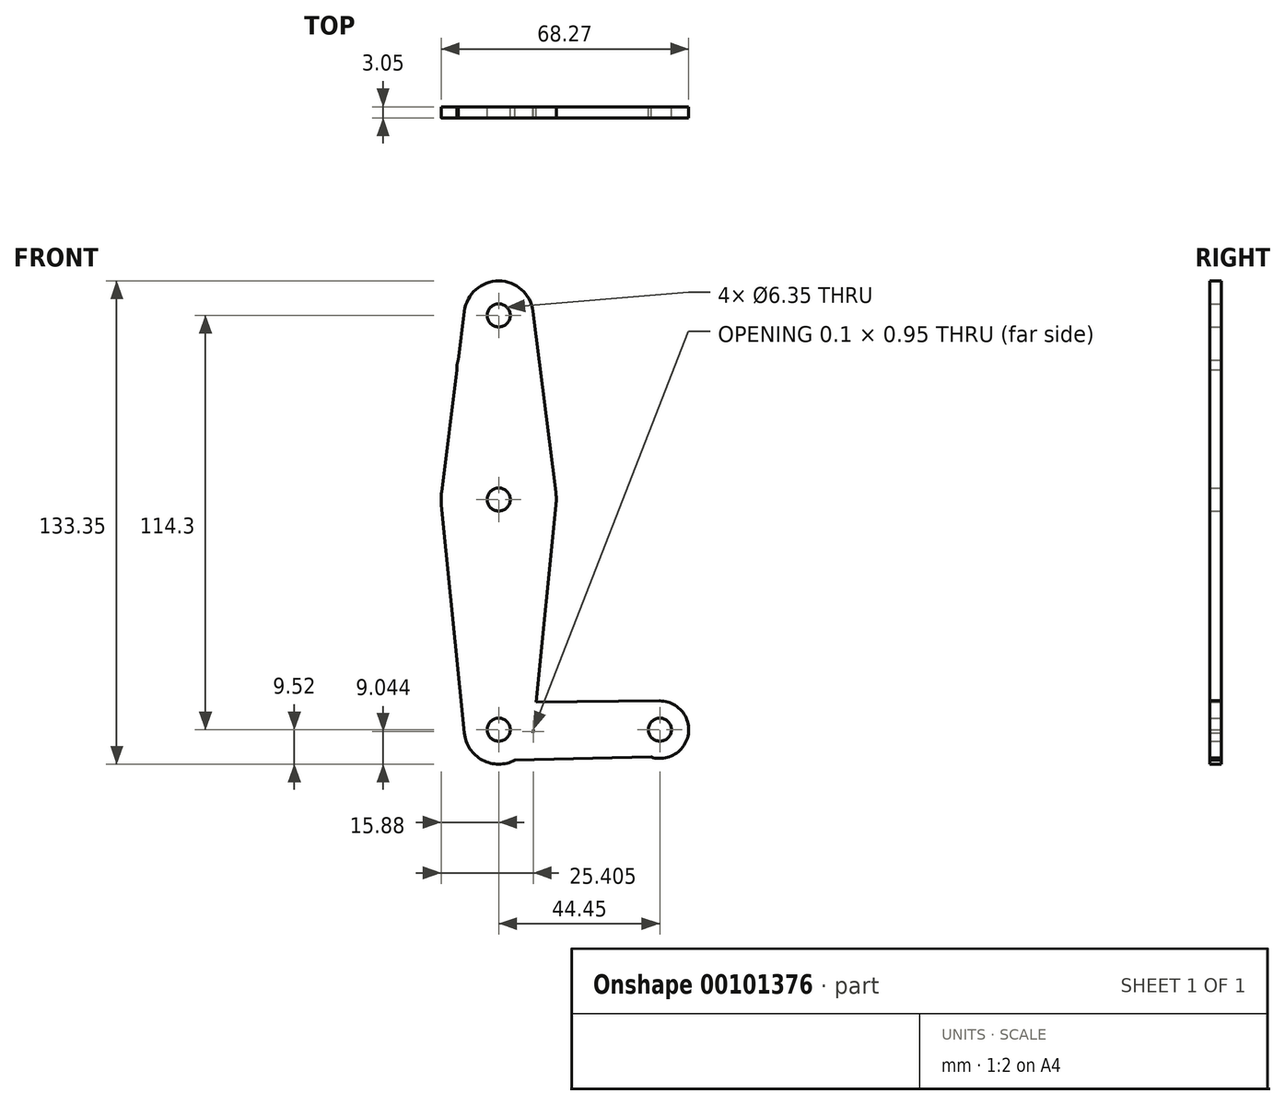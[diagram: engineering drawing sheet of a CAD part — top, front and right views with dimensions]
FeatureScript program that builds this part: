
annotation { "Feature Type Name" : "Feature", "Feature Type Description" : "" }
export const myFeature = defineFeature(function(context is Context, id is Id, definition is map)
    precondition{}
    {
        {
            var Q0;
            Q0=qCreatedBy(makeId("Front.planeOp"),FACE);
            var sketch = newSketch(context, id + "F0", { "sketchPlane" : qUnion([Q0])});
            skLineSegment(sketch, "E0", {"start": v(0, 114.3) * mm, "end": v(0, 0) * mm});
            skLineSegment(sketch, "E1", {"start": v(0, 0) * mm, "end": v(44.45, 0) * mm});
            skCircle(sketch, "E2", {"center": v(0, 114.3) * mm, "radius": 9.53 * mm});
            skCircle(sketch, "E3", {"center": v(0, 63.5) * mm, "radius": 15.88 * mm});
            skCircle(sketch, "E4", {"center": v(0, 0) * mm, "radius": 9.53 * mm});
            skCircle(sketch, "E5", {"center": v(44.45, 0) * mm, "radius": 7.94 * mm});
            skLineSegment(sketch, "E6", {"start": v(-9.45, 115.5) * mm, "end": v(-15.75, 65.48) * mm});
            skLineSegment(sketch, "E7", {"start": v(9.45, 115.5) * mm, "end": v(15.75, 65.48) * mm});
            skLineSegment(sketch, "E8", {"start": v(15.8, 61.91) * mm, "end": v(9.48, -0.95) * mm});
            skLineSegment(sketch, "E9", {"start": v(-15.8, 61.91) * mm, "end": v(-9.48, -0.95) * mm});
            skLineSegment(sketch, "E10", {"start": v(4.47, -8.41) * mm, "end": v(42.02, -7.56) * mm});
            skLineSegment(sketch, "E11", {"start": v(5.8, 7.56) * mm, "end": v(44.37, 7.94) * mm});
            skCircle(sketch, "E12", {"center": v(0, 114.3) * mm, "radius": 3.18 * mm});
            skCircle(sketch, "E13", {"center": v(0, 63.5) * mm, "radius": 3.18 * mm});
            skCircle(sketch, "E14", {"center": v(0, 0) * mm, "radius": 3.18 * mm});
            skCircle(sketch, "E15", {"center": v(44.45, 0) * mm, "radius": 3.18 * mm});
            skCircle(sketch, "E16", {"center": v(-6.35, 100.03) * mm, "radius": 5.19 * mm});
            skSolve(sketch);
        }
        {
            var Q0;
            Q0 = qSketchRegion(id + "F0", true);
            var Q1;
            {var subQ3=sQuery(id+"F0.wireOp",EDGE,"E4");var subQ6=sQuery(id+"F0.wireOp",EDGE,"E0");var subQ7=makeQuery(id+"F0.imprint","INTERSECT",VERTEX,{"derivedFrom":[subQ6,subQ3]});Q1=makeQuery(id+"F0.imprint","IMPRINT",FACE,{"disambiguationData":[TD([[makeQuery(id+"F0.imprint","IMPRINT",EDGE,{"disambiguationData":[TD([[subQ7,-1.0]])],"derivedFrom":subQ6}),1.0]])]});}
            extrude(context, id + "F1", {"entities" : qUnion([Q0, Q1]), "depth" : 3.05 * mm});
        }
    });
